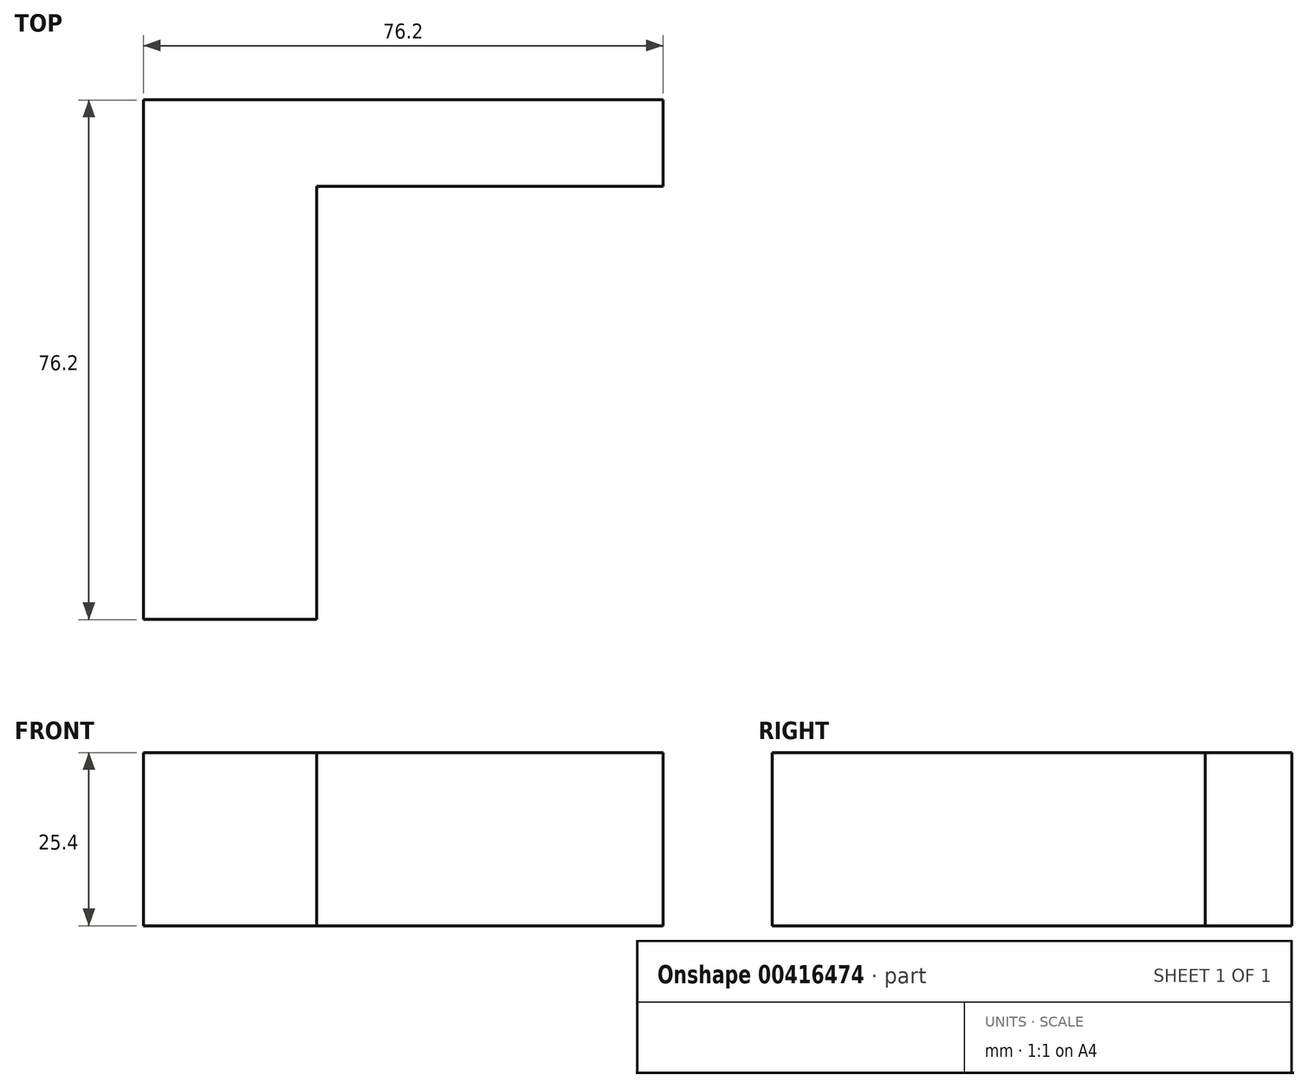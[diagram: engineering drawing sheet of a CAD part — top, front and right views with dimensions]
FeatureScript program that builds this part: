
annotation { "Feature Type Name" : "Feature", "Feature Type Description" : "" }
export const myFeature = defineFeature(function(context is Context, id is Id, definition is map)
    precondition{}
    {
        {
            var Q0;
            Q0=qCreatedBy(makeId("Top.planeOp"),FACE);
            var sketch = newSketch(context, id + "F0", { "sketchPlane" : qUnion([Q0])});
            skLineSegment(sketch, "E0", {"start": v(-40.36, -22.3) * mm, "end": v(-14.96, -22.3) * mm});
            skLineSegment(sketch, "E1", {"start": v(-14.96, -22.3) * mm, "end": v(-14.96, 53.9) * mm});
            skLineSegment(sketch, "E2", {"start": v(-14.96, 53.9) * mm, "end": v(-40.36, 53.9) * mm});
            skLineSegment(sketch, "E3", {"start": v(-40.36, 53.9) * mm, "end": v(-40.36, -22.3) * mm});
            skLineSegment(sketch, "E4", {"start": v(-40.36, -22.3) * mm, "end": v(-40.36, -22.3) * mm});
            skLineSegment(sketch, "E5", {"start": v(-14.96, 53.9) * mm, "end": v(35.84, 53.9) * mm});
            skLineSegment(sketch, "E6", {"start": v(35.84, 53.9) * mm, "end": v(35.84, 41.2) * mm});
            skLineSegment(sketch, "E7", {"start": v(35.84, 41.2) * mm, "end": v(-14.96, 41.2) * mm});
            skSolve(sketch);
        }
        {
            var Q0;
            Q0 = qSketchRegion(id + "F0", true);
            extrude(context, id + "F1", {"entities" : qUnion([Q0]), "depth" : 25.4 * mm});
        }
    });
